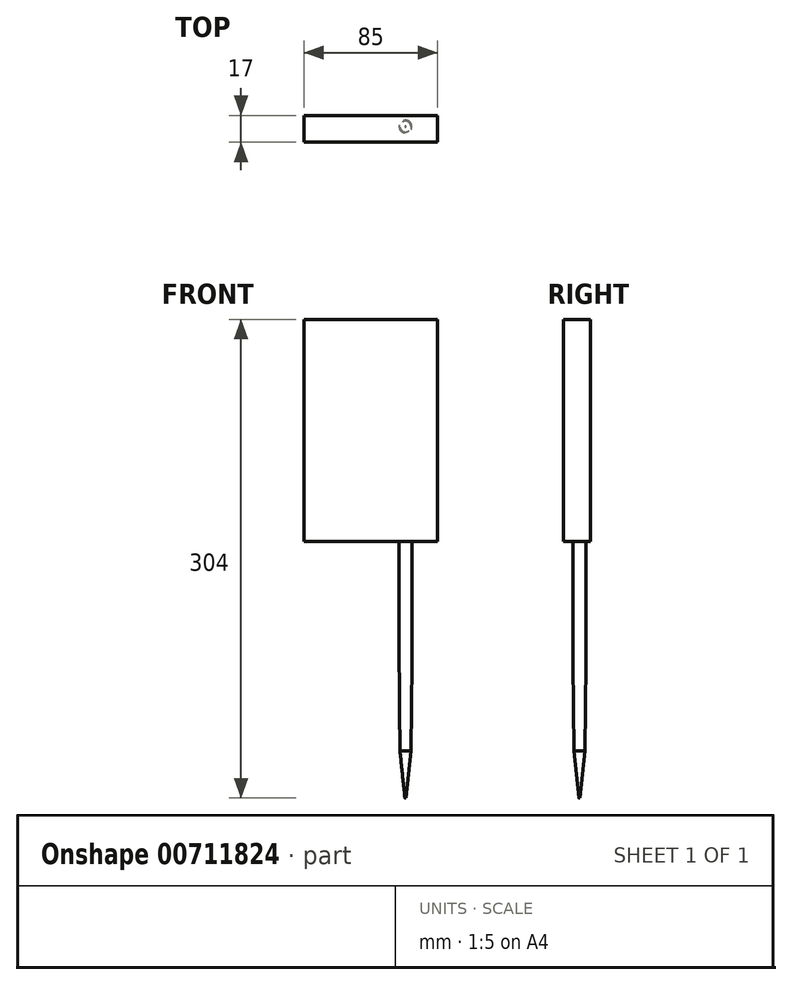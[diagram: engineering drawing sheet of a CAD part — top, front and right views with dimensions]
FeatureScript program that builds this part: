
annotation { "Feature Type Name" : "Feature", "Feature Type Description" : "" }
export const myFeature = defineFeature(function(context is Context, id is Id, definition is map)
    precondition{}
    {
        {
            var Q0;
            Q0=qCreatedBy(makeId("Front.planeOp"),FACE);
            var sketch = newSketch(context, id + "F0", { "sketchPlane" : qUnion([Q0])});
            skLineSegment(sketch, "E0.bottom", {"start": v(0, 0) * mm, "end": v(85, 0) * mm});
            skLineSegment(sketch, "E0.top", {"start": v(0, 141.1) * mm, "end": v(85, 141.1) * mm});
            skLineSegment(sketch, "E0.left", {"start": v(0, 0) * mm, "end": v(0, 141.1) * mm});
            skLineSegment(sketch, "E0.right", {"start": v(85, 0) * mm, "end": v(85, 141.1) * mm});
            skSolve(sketch);
        }
        {
            var Q0;
            Q0=makeQuery(id+"F0.imprint","IMPRINT",FACE,{"disambiguationData":[TD([[makeQuery(id+"F0.imprint","IMPRINT",EDGE,{"derivedFrom":sQuery(id+"F0.wireOp",EDGE,"E0.bottom")}),1.0]])]});
            extrude(context, id + "F1", {"entities" : qUnion([Q0]), "depth" : 17 * mm, "offsetDistance" : 25 * mm});
        }
        {
            var Q0;
            Q0=makeQuery(id+"F1.opExtrude","SWEPT_FACE",FACE,{"disambiguationData":[OSD([sQuery(id+"F0.wireOp",EDGE,"E0.bottom")])]});
            var sketch = newSketch(context, id + "F2", { "sketchPlane" : qUnion([Q0])});
            skCircle(sketch, "E1", {"center": v(64.5, 7) * mm, "radius": 4 * mm});
            skSolve(sketch);
        }
        {
            var Q0;
            Q0 = qSketchRegion(id + "F2", true);
            extrude(context, id + "F3", {"entities" : qUnion([Q0]), "operationType" : NewBodyOperationType.ADD, "depth" : 77 * mm, "offsetDistance" : 25 * mm});
        }
        {
            var Q0;
            Q0=makeQuery(id+"F3.opExtrude","CAP_FACE",FACE,{"disambiguationData":[OSD([sQuery(id+"F2.wireOp",EDGE,"E1")])],"isStart":false});
            var sketch = newSketch(context, id + "F4", { "sketchPlane" : qUnion([Q0])});
            skCircle(sketch, "E2", {"center": v(64.5, 7) * mm, "radius": 4 * mm});
            skSolve(sketch);
        }
        {
            var Q0;
            Q0 = qSketchRegion(id + "F4", true);
            extrude(context, id + "F5", {"entities" : qUnion([Q0]), "operationType" : NewBodyOperationType.ADD, "depth" : 55.9 * mm, "offsetDistance" : 25 * mm, "hasDraft" : true, "draftAngle" : 0.5 * degree, "draftPullDirection" : true});
        }
        {
            var Q0;
            Q0=makeQuery(id+"F5.opExtrude","CAP_FACE",FACE,{"disambiguationData":[OSD([sQuery(id+"F4.wireOp",EDGE,"E2")])],"isStart":false});
            var sketch = newSketch(context, id + "F6", { "sketchPlane" : qUnion([Q0])});
            skCircle(sketch, "E3", {"center": v(64.5, 7) * mm, "radius": 3.51 * mm});
            skSolve(sketch);
        }
        {
            var Q0;
            Q0 = qSketchRegion(id + "F6", true);
            extrude(context, id + "F7", {"entities" : qUnion([Q0]), "operationType" : NewBodyOperationType.ADD, "depth" : 30 * mm, "offsetDistance" : 25 * mm, "hasDraft" : true, "draftAngle" : 6 * degree, "draftPullDirection" : true});
        }
    });
